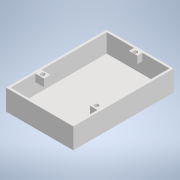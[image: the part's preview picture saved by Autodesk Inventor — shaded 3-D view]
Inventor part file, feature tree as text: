
AUTODESK INVENTOR PART (.ipt)
format: ipt  version: 2022 (Build 260153000, 153)  size: 165,888 bytes
history: native  units: mm
features: sketch x6, extrude x5, other x4, reference x4, projected_geometry x2
ambient origin geometry x8: Origin, YZ Plane, XZ Plane, XY Plane, X Axis, Y Axis, Z Axis, Center Point
bodies: Body1 (feature_tree)
feature tree (21):
  other  "Твердое тело1"
  extrude  "Выдавливание1"  Depth=200.0mm
  extrude  "Выдавливание2"  Depth=200.0mm
  extrude  "Выдавливание3"  Depth=3.0mm TaperAngle=0.0deg
  extrude  "Выдавливание4"  Depth=3.0mm TaperAngle=0.0deg
  sketch  "Эскиз5"
  extrude  "Выдавливание5"  Depth=3.0mm
  sketch  "Эскиз1"
  sketch  "Эскиз2"
  projected_geometry  "Спроецированная петля1"
  sketch  "Эскиз3"
  projected_geometry  "Спроецированная петля2"
  sketch  "Эскиз4"
  reference  "Ссылка1"
  sketch  "Эскиз6"
  reference  "Ссылка2"
  reference  "Ссылка3"
  reference  "Ссылка4"
  other  "Сборка2"
  other  "Hold_18650-4:1"
  other  "goruntu modulu:1"
